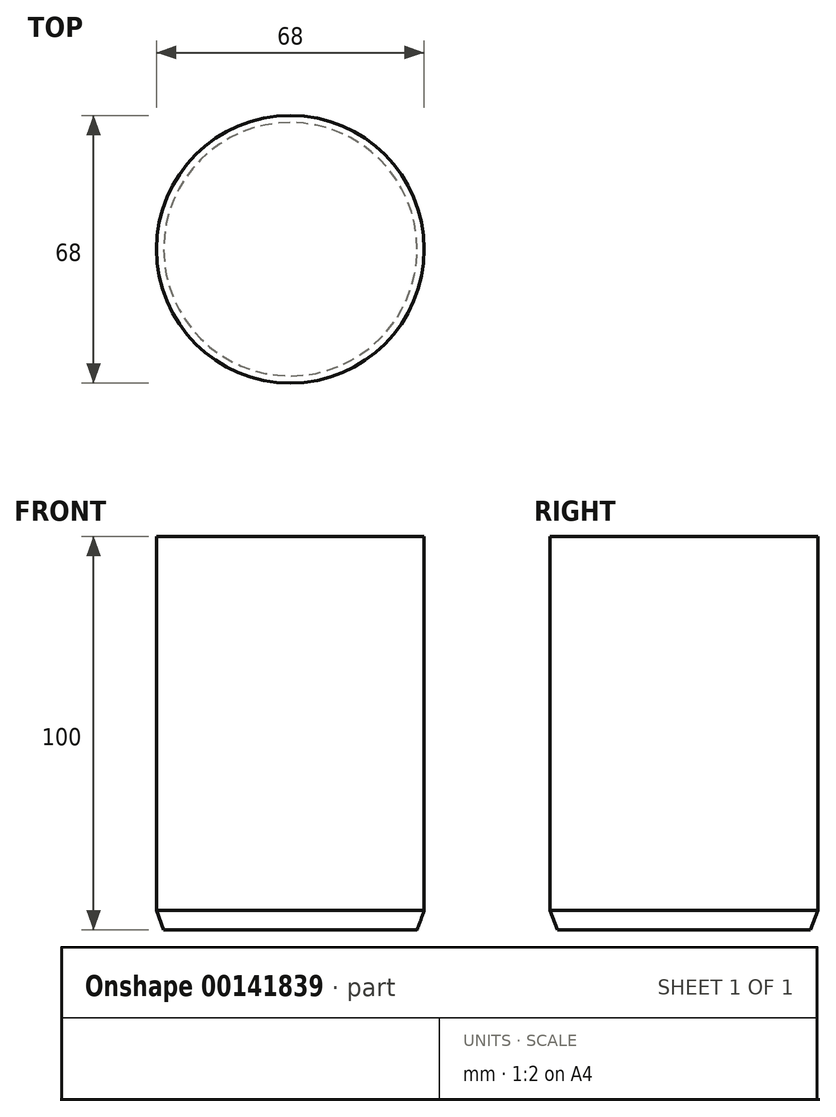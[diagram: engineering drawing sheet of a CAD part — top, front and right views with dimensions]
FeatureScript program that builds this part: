
annotation { "Feature Type Name" : "Feature", "Feature Type Description" : "" }
export const myFeature = defineFeature(function(context is Context, id is Id, definition is map)
    precondition{}
    {
        {
            var Q0;
            Q0=qCreatedBy(makeId("Front.planeOp"),FACE);
            var sketch = newSketch(context, id + "F0", { "sketchPlane" : qUnion([Q0])});
            skLineSegment(sketch, "E0", {"start": v(0, 50) * mm, "end": v(0, -50) * mm});
            skLineSegment(sketch, "E1", {"start": v(0, -50) * mm, "end": v(-32.18, -50) * mm});
            skLineSegment(sketch, "E2", {"start": v(-32.18, -50) * mm, "end": v(-34, -45) * mm});
            skLineSegment(sketch, "E3", {"start": v(-34, -45) * mm, "end": v(-34, 50) * mm});
            skLineSegment(sketch, "E4", {"start": v(-34, 50) * mm, "end": v(0, 50) * mm});
            skSolve(sketch);
        }
        {
            var Q0;
            Q0=makeQuery(id+"F0.imprint","IMPRINT",FACE,{"disambiguationData":[TD([[makeQuery(id+"F0.imprint","IMPRINT",EDGE,{"derivedFrom":sQuery(id+"F0.wireOp",EDGE,"E0")}),-1.0]])]});
            var Q1;
            Q1=sQuery(id+"F0.wireOp",EDGE,"E0");
            revolve(context, id + "F1", {"entities" : qUnion([Q0]), "axis" : qUnion([Q1]), "revolveType" : RevolveType.FULL});
        }
    });
